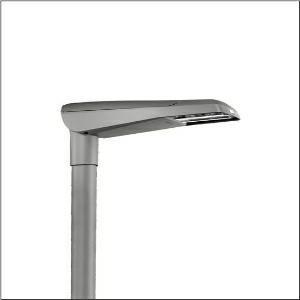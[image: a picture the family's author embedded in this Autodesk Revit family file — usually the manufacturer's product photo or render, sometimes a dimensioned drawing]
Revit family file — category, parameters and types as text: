
# Revit family: streetlight_sl_11_iq_micro___st1_2a_5xc1ac1f08de_2d80
name_source: partatom
category: Lighting Fixtures
units: mm (PartAtom-declared; Revit-internal decimal feet)

## family parameters
Cut with Voids When Loaded = No
Host = Face
Light Source = No
Part Type = Normal
Room Calculation Point = No
Round Connector Dimension = Use Diameter
Shared = No

## types (1)
- --- (1 x LED, 3860 lm, 27.4 W, 4000K)
    Apparent Load = 27 VA
    CIE Flux Codes = 33 71 96 100 100
    Color Rendering = 70
    Color Temperature = 4000K
    Default Elevation = 1800 mm
    Description = Streetlight SL 11 iQ micro, mast luminaire, primary light control with 3 zone facetted reflector, of plastic, silver coated, highly specular, primary optical cover: cover, of PMMA, transparent, light distribution: ST1.2a, light emission: direct distribution, primary light characteristic: asymmetric, installation type: post-top, side-entry, LED, High Power LED, rated luminous flux: 3.620lm, luminous efficacy: 131lm/W, light colour: 722/727/730/740, colour temperature: 2200/2700/3000/4000K, control gear: iQ Street-Remote, control: Street-Remote, Auto-Match, Temp-Guard, Lumen-Switch, Night-Set, Smart-Wire, Light-Fading, Desk-Remote (wireless, voltage-free reading and setting of iQ features in the workshop via application-optimized NFC function/RFID function), optimised constant luminous flux control (CLO 2.0), with cable H07RN-F 5x 1.5mm², mains connection: 220..240V, AC, 50/60Hz, connection cable pre-assembled, cable length: 6,5m, start of lifetime: 28W, end of service life: 28W, reduction: 13W, luminaire housing, of diecast aluminium, powder-coated, Siteco® metallic grey (DB 702S), please order mast flange separately, inclination adjustable without tools: 0°, 5°, 10°, 15° (post-top) | 0°, -5°, -10°, -15° (side-entry), sealing non-destructively replaceable, multi-level sealing system, length: 600mm, width: 174mm, height: 116mm, mast flange for spigot size: 42mm (side-entry): 5XC10008XM4, 60/48mm (side-entry/post-top): 5XC10108XM2, 76/60mm (side-entry/post-top): 5XC10108XM1, mounting height: 4..8m, equipment: Power, protection rating (complete): IP66, insulation class (complete): insulation class II (safety insulation), certification: CE, ENEC, VDE, impact resistance: IK09, permissible operating ambient temperature for outdoor applications: -25..+50°C, standard-compliant lighting for roads and squares, Environmental Product Declaration (EPD) tested and certified by an independent institute, packaging unit: 1 piece

Light Distribution: ST1.2a
    Height = 116 mm
    Lamp = 1 x LED
    Lamp Light Flux = 3860 lm
    Lamp Power = 27.4 W
    Lamp count = 1
    Length = 600 mm
    Luminous efficacy = 141 lm/W
    Manufacturer = Siteco
    ModVariant = No
    Model = 5XC1AC1F08DE
    Number of Poles = 1
    OnlyDefault = Yes
    Power Factor = 1
    Product Name = Streetlight SL 11 iQ micro | ST1.2a
    Product group = mast luminaire | pylon top
    ProductGroupID = 6100
    Protection Class = Protection class II
    Protection Degree = IP 66
    RLX_Detail_Level = 1
    RLX_Emergency_Light_Flux = 0 lm
    RLX_Emergency_Type = 0
    RLX_Emergency_Type_DB = No
    RlxData = <blob elided: 59421 chars, md5=fcfe2473>
    Socket = socket
    Standby Power = 0 W
    System Light Flux = 3860 lm
    System Power = 27 W
    Type Comments = individual setting: luminous flux: 100 % | dim-lin: 254 | 726 mA
    Type Image = l_1006566.jpg
    URL = http://relux.com
    VarID = @adj_037436
    Voltage = 0 V
    Weight = 0.00 kg
    Width = 174 mm

## geometry (parser evidence)
native form markers: Blend x4, Sweep x11
no freeform markers — native parametric forms only
